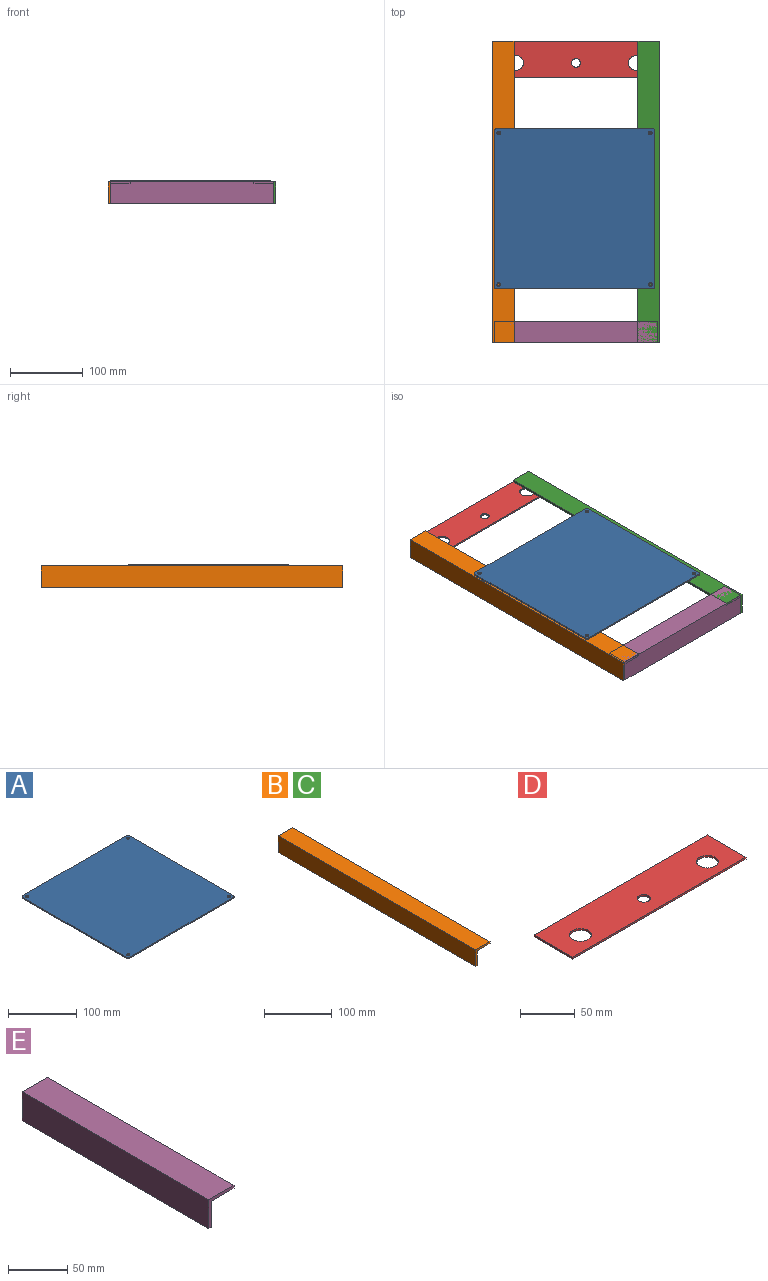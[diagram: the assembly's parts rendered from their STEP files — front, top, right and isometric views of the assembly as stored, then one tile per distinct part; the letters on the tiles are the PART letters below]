
ASSEMBLY  parts=5 mates=4
PART A: 22 faces, bbox 220x220x2 mm
  f0: cylinder r=1.5mm len=3mm, axis (0,0,-1), area 3.8mm2, adj f9,f16
  f1: cylinder r=1.5mm len=3mm, axis (0,0,-1), area 3.8mm2, adj f9,f14
  f2: cylinder r=1.5mm len=3mm, axis (0,0,-1), area 3.8mm2, adj f9,f20
  f3: cylinder r=1.5mm len=3mm, axis (0,0,-1), area 3.8mm2, adj f9,f18
  f4: plane 214x2mm, normal (1,0,0), area 428mm2, adj f8,f9,f10,f13
  f5: plane 214x2mm, normal (0,1,0), area 428mm2, adj f8,f9,f10,f11
  f6: plane 214x2mm, normal (-1,0,0), area 428mm2, adj f8,f9,f11,f12
  f7: plane 214x2mm, normal (0,-1,0), area 428mm2, adj f8,f9,f12,f13
  f8: plane 220x220mm, normal (0,0,1), area 48313.7mm2, adj f4,f5,f6,f7,f10,f11,f12,f13
  f9: plane 220x220mm, normal (0,0,-1), area 48364mm2, adj f0,f1,f2,f3,f4,f5,f6,f7
  f10: cylinder r=3mm len=3mm, axis (0,0,1), area 9.4mm2, adj f4,f5,f8,f9
  f11: cylinder r=3mm len=3mm, axis (0,0,-1), area 9.4mm2, adj f5,f6,f8,f9
  f12: cylinder r=3mm len=3mm, axis (0,0,1), area 9.4mm2, adj f6,f7,f8,f9
  f13: cylinder r=3mm len=3mm, axis (0,0,-1), area 9.4mm2, adj f4,f7,f8,f9
  f14: cone r=0mm half-angle=59deg, axis (0,0,1), area 14.7mm2, adj f1,f15
  f15: cylinder r=2.5mm len=5mm, axis (0,0,1), area 15.7mm2, adj f8,f14
  f16: cone r=0mm half-angle=59deg, axis (0,0,1), area 14.7mm2, adj f0,f17
  f17: cylinder r=2.5mm len=5mm, axis (0,0,1), area 15.7mm2, adj f8,f16
  f18: cone r=0mm half-angle=59deg, axis (0,0,1), area 14.7mm2, adj f3,f19
  f19: cylinder r=2.5mm len=5mm, axis (0,0,1), area 15.7mm2, adj f8,f18
  f20: cone r=0mm half-angle=59deg, axis (0,0,1), area 14.7mm2, adj f2,f21
  f21: cylinder r=2.5mm len=5mm, axis (0,0,1), area 15.7mm2, adj f8,f20
PART B: 8 faces, bbox 30x414x30 mm
  f0: plane 414x30mm, normal (0,0,1), area 12420mm2, adj f1,f5,f6,f7
  f1: plane 414x30mm, normal (-1,0,0), area 12420mm2, adj f0,f2,f6,f7
  f2: plane 414x3mm, normal (0,0,-1), area 1242mm2, adj f1,f3,f6,f7
  f3: plane 414x27mm, normal (1,0,0), area 11178mm2, adj f2,f4,f6,f7
  f4: plane 414x27mm, normal (0,0,-1), area 11178mm2, adj f3,f5,f6,f7
  f5: plane 414x3mm, normal (1,0,0), area 1242mm2, adj f0,f4,f6,f7
  f6: plane 30x30mm, normal (0,-1,0), area 171mm2, adj f0,f1,f2,f3,f4,f5
  f7: plane 30x30mm, normal (0,1,0), area 171mm2, adj f0,f1,f2,f3,f4,f5
PART C: same geometry as B
PART D: 9 faces, bbox 224x50x2 mm
  f0: plane 50x2mm, normal (1,0,0), area 100mm2, adj f1,f5,f7,f8
  f1: plane 224x2mm, normal (0,1,0), area 448mm2, adj f0,f2,f7,f8
  f2: plane 50x2mm, normal (-1,0,0), area 100mm2, adj f1,f5,f7,f8
  f3: cylinder r=10mm len=20mm, axis (0,0,-1), area 125.7mm2, adj f7,f8
  f4: cylinder r=6mm len=12mm, axis (0,0,-1), area 75.4mm2, adj f7,f8
  f5: plane 224x2mm, normal (0,-1,0), area 448mm2, adj f0,f2,f7,f8
  f6: cylinder r=10mm len=20mm, axis (0,0,-1), area 125.7mm2, adj f7,f8
  f7: plane 224x50mm, normal (0,0,1), area 10458.6mm2, adj f0,f1,f2,f3,f4,f5,f6
  f8: plane 224x50mm, normal (0,0,-1), area 10458.6mm2, adj f0,f1,f2,f3,f4,f5,f6
PART E: 8 faces, bbox 30x224x30 mm
  f0: plane 224x30mm, normal (0,0,1), area 6720mm2, adj f1,f5,f6,f7
  f1: plane 224x30mm, normal (-1,0,0), area 6720mm2, adj f0,f2,f6,f7
  f2: plane 224x3mm, normal (0,0,-1), area 672mm2, adj f1,f3,f6,f7
  f3: plane 224x27mm, normal (1,0,0), area 6048mm2, adj f2,f4,f6,f7
  f4: plane 224x27mm, normal (0,0,-1), area 6048mm2, adj f3,f5,f6,f7
  f5: plane 224x3mm, normal (1,0,0), area 672mm2, adj f0,f4,f6,f7
  f6: plane 30x30mm, normal (0,-1,0), area 171mm2, adj f0,f1,f2,f3,f4,f5
  f7: plane 30x30mm, normal (0,1,0), area 171mm2, adj f0,f1,f2,f3,f4,f5
PLACE A at identity fixed
PLACE B t=(-113,230,0)mm
PLACE C rot(axis=(0,1,0),90deg) t=(117,230,0)mm
PLACE D rot(axis=(0,1,0),180deg) t=(2,200,-3)mm
PLACE E rot(axis=(0,0,1),90deg) t=(-110,-184,0)mm
MATE fastened C.f3 <-> D.f8  axis (0,0,-1) through (114,230,-3)mm
MATE fastened E.f0 <-> C.f1  axis (0,0,1) through (114,-184,0)mm
MATE fastened D.f8 <-> B.f4  axis (0,0,1) through (-110,230,-3)mm
MATE fastened C.f1 <-> A.f9  axis (0,0,1) through (102,-184,0)mm
